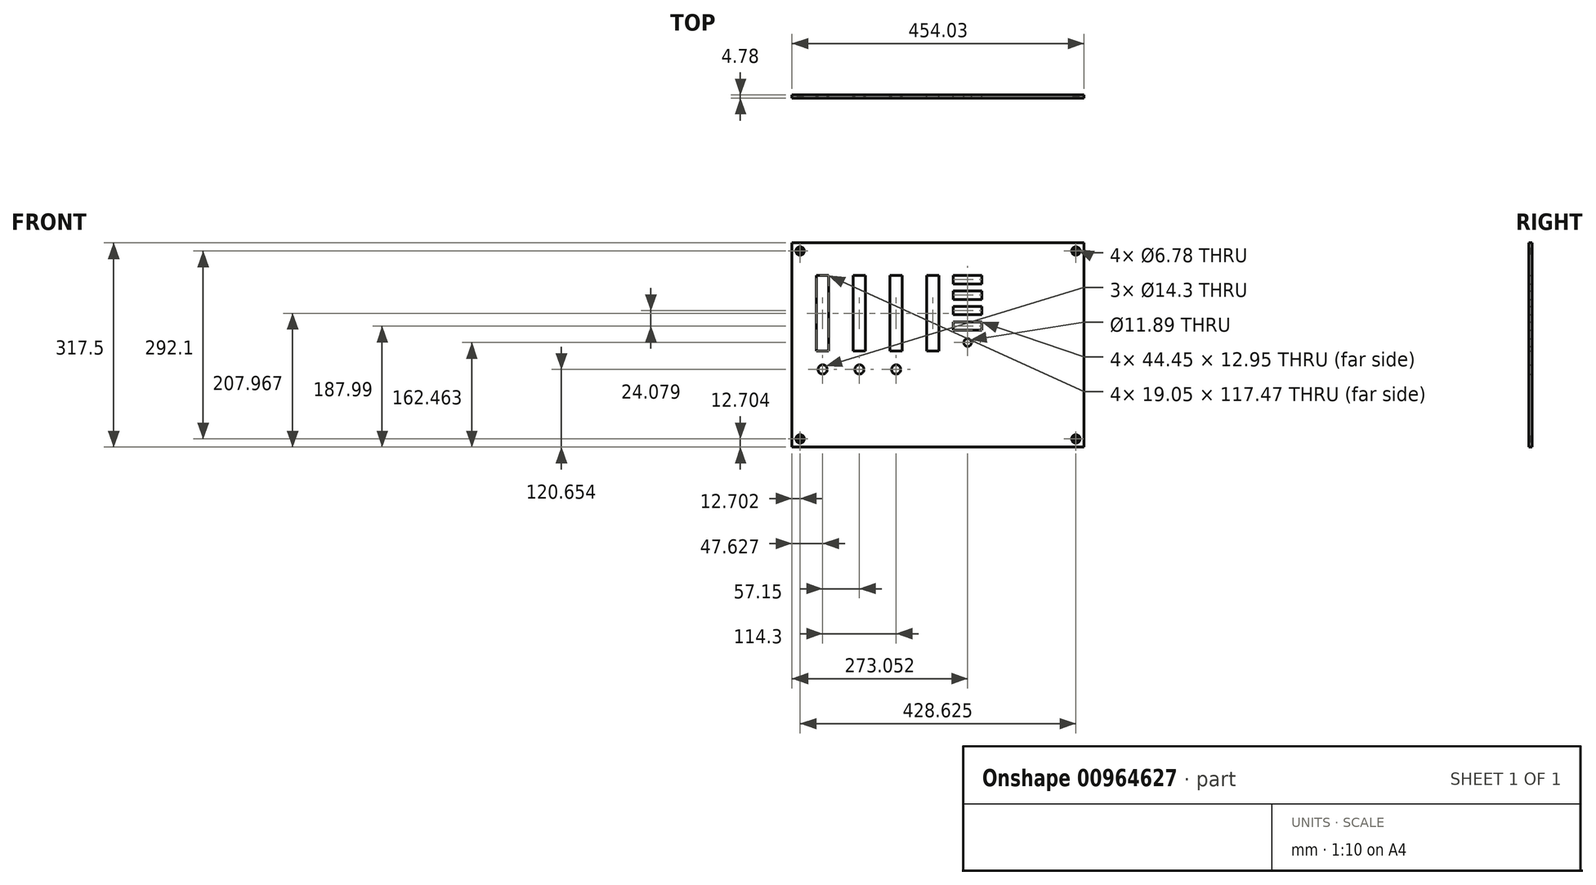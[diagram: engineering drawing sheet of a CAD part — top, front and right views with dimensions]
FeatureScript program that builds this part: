
annotation { "Feature Type Name" : "Feature", "Feature Type Description" : "" }
export const myFeature = defineFeature(function(context is Context, id is Id, definition is map)
    precondition{}
    {
        {
            var Q0;
            Q0=qCreatedBy(makeId("Front.planeOp"),FACE);
            var sketch = newSketch(context, id + "F0", { "sketchPlane" : qUnion([Q0])});
            skLineSegment(sketch, "E0.bottom", {"start": v(-161.53, 204.21) * mm, "end": v(292.5, 204.21) * mm});
            skLineSegment(sketch, "E0.top", {"start": v(-161.53, -113.29) * mm, "end": v(292.5, -113.29) * mm});
            skLineSegment(sketch, "E0.left", {"start": v(-161.53, 204.21) * mm, "end": v(-161.53, -113.29) * mm});
            skLineSegment(sketch, "E0.right", {"start": v(292.5, 204.21) * mm, "end": v(292.5, -113.29) * mm});
            skLineSegment(sketch, "E1.bottom", {"start": v(-123.43, 153.41) * mm, "end": v(-104.38, 153.41) * mm});
            skLineSegment(sketch, "E1.top", {"start": v(-123.43, 35.94) * mm, "end": v(-104.38, 35.94) * mm});
            skLineSegment(sketch, "E1.left", {"start": v(-123.43, 153.41) * mm, "end": v(-123.43, 35.94) * mm});
            skLineSegment(sketch, "E1.right", {"start": v(-104.38, 153.41) * mm, "end": v(-104.38, 35.94) * mm});
            skLineSegment(sketch, "E2.bottom", {"start": v(-66.28, 153.41) * mm, "end": v(-47.23, 153.41) * mm});
            skLineSegment(sketch, "E2.top", {"start": v(-66.28, 35.94) * mm, "end": v(-47.23, 35.94) * mm});
            skLineSegment(sketch, "E2.left", {"start": v(-66.28, 153.41) * mm, "end": v(-66.28, 35.94) * mm});
            skLineSegment(sketch, "E2.right", {"start": v(-47.23, 153.41) * mm, "end": v(-47.23, 35.94) * mm});
            skLineSegment(sketch, "E3.bottom", {"start": v(-9.13, 153.41) * mm, "end": v(9.92, 153.41) * mm});
            skLineSegment(sketch, "E3.top", {"start": v(-9.13, 35.94) * mm, "end": v(9.92, 35.94) * mm});
            skLineSegment(sketch, "E3.left", {"start": v(-9.13, 153.41) * mm, "end": v(-9.13, 35.94) * mm});
            skLineSegment(sketch, "E3.right", {"start": v(9.92, 153.41) * mm, "end": v(9.92, 35.94) * mm});
            skLineSegment(sketch, "E4.bottom", {"start": v(48.02, 153.41) * mm, "end": v(67.07, 153.41) * mm});
            skLineSegment(sketch, "E4.top", {"start": v(48.02, 35.94) * mm, "end": v(67.07, 35.94) * mm});
            skLineSegment(sketch, "E4.left", {"start": v(48.02, 153.41) * mm, "end": v(48.02, 35.94) * mm});
            skLineSegment(sketch, "E4.right", {"start": v(67.07, 153.41) * mm, "end": v(67.07, 35.94) * mm});
            skLineSegment(sketch, "E5.bottom", {"start": v(89.3, 153.41) * mm, "end": v(133.75, 153.41) * mm});
            skLineSegment(sketch, "E5.top", {"start": v(89.3, 140.46) * mm, "end": v(133.75, 140.46) * mm});
            skLineSegment(sketch, "E5.left", {"start": v(89.3, 153.41) * mm, "end": v(89.3, 140.46) * mm});
            skLineSegment(sketch, "E5.right", {"start": v(133.75, 153.41) * mm, "end": v(133.75, 140.46) * mm});
            skLineSegment(sketch, "E6.bottom", {"start": v(89.3, 129.33) * mm, "end": v(133.75, 129.33) * mm});
            skLineSegment(sketch, "E6.top", {"start": v(89.3, 116.38) * mm, "end": v(133.75, 116.38) * mm});
            skLineSegment(sketch, "E6.left", {"start": v(89.3, 129.33) * mm, "end": v(89.3, 116.38) * mm});
            skLineSegment(sketch, "E6.right", {"start": v(133.75, 129.33) * mm, "end": v(133.75, 116.38) * mm});
            skLineSegment(sketch, "E7.bottom", {"start": v(89.3, 105.26) * mm, "end": v(133.75, 105.26) * mm});
            skLineSegment(sketch, "E7.top", {"start": v(89.3, 92.3) * mm, "end": v(133.75, 92.3) * mm});
            skLineSegment(sketch, "E7.left", {"start": v(89.3, 105.26) * mm, "end": v(89.3, 92.3) * mm});
            skLineSegment(sketch, "E7.right", {"start": v(133.75, 105.26) * mm, "end": v(133.75, 92.3) * mm});
            skLineSegment(sketch, "E8.bottom", {"start": v(89.3, 81.18) * mm, "end": v(133.75, 81.18) * mm});
            skLineSegment(sketch, "E8.top", {"start": v(89.3, 68.22) * mm, "end": v(133.75, 68.22) * mm});
            skLineSegment(sketch, "E8.left", {"start": v(89.3, 81.18) * mm, "end": v(89.3, 68.22) * mm});
            skLineSegment(sketch, "E8.right", {"start": v(133.75, 81.18) * mm, "end": v(133.75, 68.22) * mm});
            skCircle(sketch, "E9", {"center": v(111.52, 49.17) * mm, "radius": 5.94 * mm});
            skPoint(sketch, "E10.endSnap0", {"position": v(111.52, 68.22) * mm});
            skCircle(sketch, "E11", {"center": v(-113.9, 7.36) * mm, "radius": 7.15 * mm});
            skCircle(sketch, "E12", {"center": v(-56.75, 7.36) * mm, "radius": 7.15 * mm});
            skCircle(sketch, "E13", {"center": v(0.4, 7.36) * mm, "radius": 7.15 * mm});
            skLineSegment(sketch, "E14.bottom", {"start": v(-148.83, 191.51) * mm, "end": v(279.8, 191.51) * mm, "construction": true});
            skLineSegment(sketch, "E14.top", {"start": v(-148.83, -100.59) * mm, "end": v(279.8, -100.59) * mm, "construction": true});
            skLineSegment(sketch, "E14.left", {"start": v(-148.83, 191.51) * mm, "end": v(-148.83, -100.59) * mm, "construction": true});
            skLineSegment(sketch, "E14.right", {"start": v(279.8, 191.51) * mm, "end": v(279.8, -100.59) * mm, "construction": true});
            skCircle(sketch, "E15", {"center": v(-148.83, -100.59) * mm, "radius": 3.4 * mm});
            skCircle(sketch, "E16", {"center": v(-148.83, 191.51) * mm, "radius": 3.4 * mm});
            skCircle(sketch, "E17", {"center": v(279.8, 191.51) * mm, "radius": 3.4 * mm});
            skCircle(sketch, "E18", {"center": v(279.8, -100.59) * mm, "radius": 3.4 * mm});
            skLineSegment(sketch, "E19", {"start": v(-113.9, 7.36) * mm, "end": v(33.97, 7.36) * mm, "construction": true});
            skLineSegment(sketch, "E20", {"start": v(-113.9, 7.36) * mm, "end": v(-132.64, 7.36) * mm, "construction": true});
            skSolve(sketch);
        }
        {
            var Q0;
            Q0=makeQuery(id+"F0.imprint","IMPRINT",FACE,{"disambiguationData":[TD([[makeQuery(id+"F0.imprint","IMPRINT",EDGE,{"derivedFrom":sQuery(id+"F0.wireOp",EDGE,"E0.bottom")}),-1.0]])]});
            extrude(context, id + "F1", {"entities" : qUnion([Q0]), "depth" : 4.78 * mm, "offsetDistance" : 25.4 * mm});
        }
        {
            var Q0;
            Q0=makeQuery(id+"F1.opExtrude","CAP_EDGE",EDGE,{"disambiguationData":[OSD([sQuery(id+"F0.wireOp",EDGE,"E15")])],"isStart":false});
            var Q1;
            Q1=makeQuery(id+"F1.opExtrude","CAP_EDGE",EDGE,{"disambiguationData":[OSD([sQuery(id+"F0.wireOp",EDGE,"E18")])],"isStart":false});
            var Q2;
            Q2=makeQuery(id+"F1.opExtrude","CAP_EDGE",EDGE,{"disambiguationData":[OSD([sQuery(id+"F0.wireOp",EDGE,"E17")])],"isStart":false});
            var Q3;
            Q3=makeQuery(id+"F1.opExtrude","CAP_EDGE",EDGE,{"disambiguationData":[OSD([sQuery(id+"F0.wireOp",EDGE,"E16")])],"isStart":false});
            chamfer(context, id + "F2", {"entities" : qUnion([Q0, Q1, Q2, Q3]), "width" : 3.17 * mm, "tangentPropagation" : true});
        }
    });
